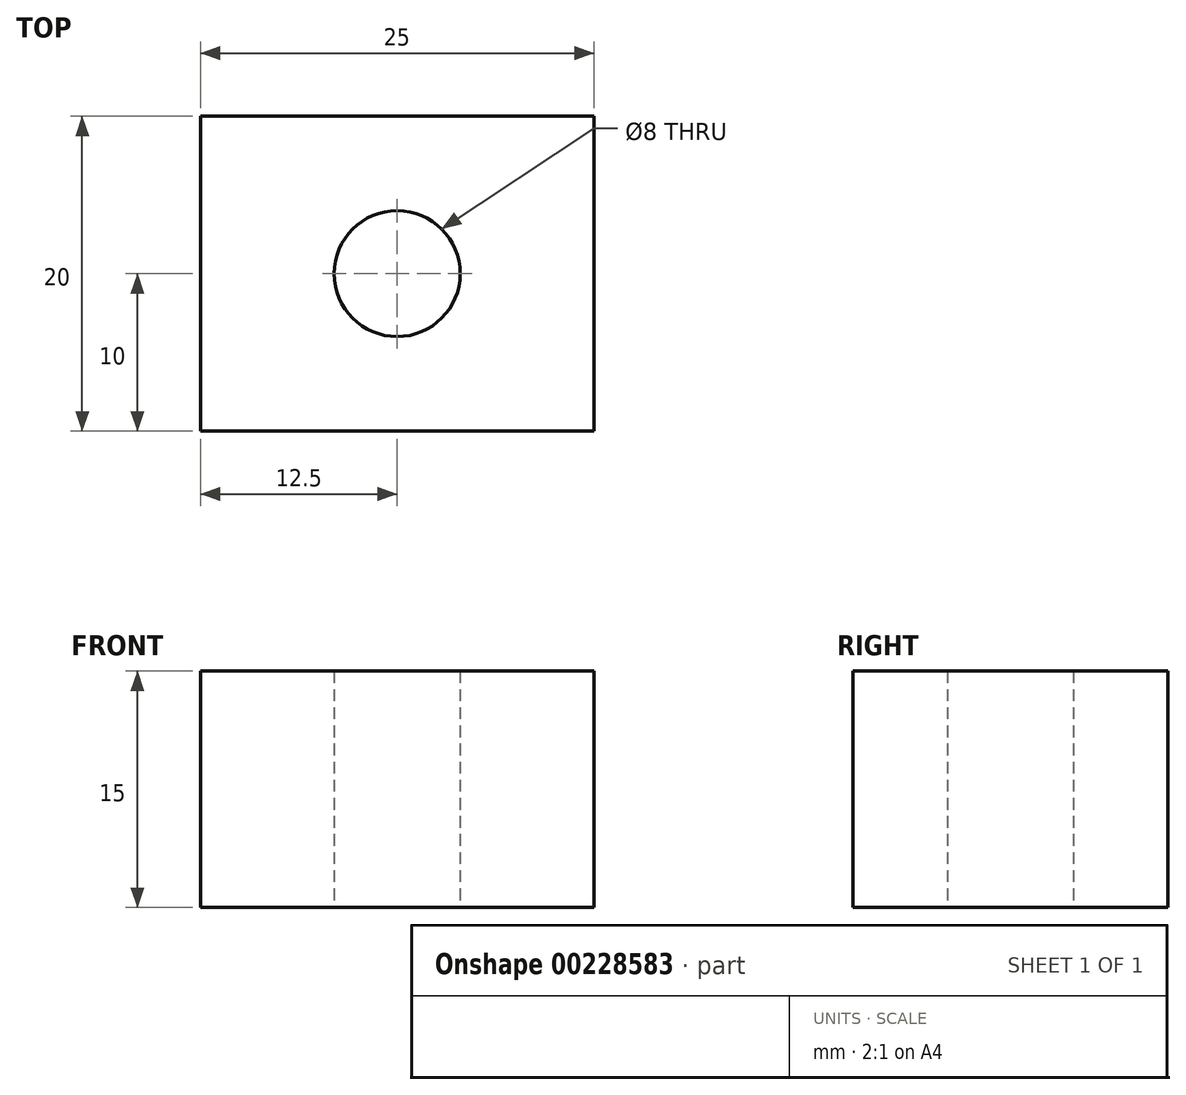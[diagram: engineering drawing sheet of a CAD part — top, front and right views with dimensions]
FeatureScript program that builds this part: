
annotation { "Feature Type Name" : "Feature", "Feature Type Description" : "" }
export const myFeature = defineFeature(function(context is Context, id is Id, definition is map)
    precondition{}
    {
        {
            var Q0;
            Q0=qCreatedBy(makeId("Top.planeOp"),FACE);
            var sketch = newSketch(context, id + "F0", { "sketchPlane" : qUnion([Q0])});
            skLineSegment(sketch, "E0.bottom", {"start": v(0, 0) * mm, "end": v(25, 0) * mm});
            skLineSegment(sketch, "E0.top", {"start": v(0, 20) * mm, "end": v(25, 20) * mm});
            skLineSegment(sketch, "E0.left", {"start": v(0, 0) * mm, "end": v(0, 20) * mm});
            skLineSegment(sketch, "E0.right", {"start": v(25, 0) * mm, "end": v(25, 20) * mm});
            skCircle(sketch, "E1", {"center": v(12.5, 10) * mm, "radius": 4 * mm});
            skLineSegment(sketch, "E2", {"start": v(12.5, 10) * mm, "end": v(12.5, 0) * mm, "construction": true});
            skLineSegment(sketch, "E3", {"start": v(12.5, 10) * mm, "end": v(25, 10) * mm, "construction": true});
            skSolve(sketch);
        }
        {
            var Q0;
            Q0=makeQuery(id+"F0.imprint","IMPRINT",FACE,{"disambiguationData":[TD([[makeQuery(id+"F0.imprint","IMPRINT",EDGE,{"derivedFrom":sQuery(id+"F0.wireOp",EDGE,"E0.bottom")}),1.0]])]});
            extrude(context, id + "F1", {"entities" : qUnion([Q0]), "depth" : 15 * mm});
        }
    });
